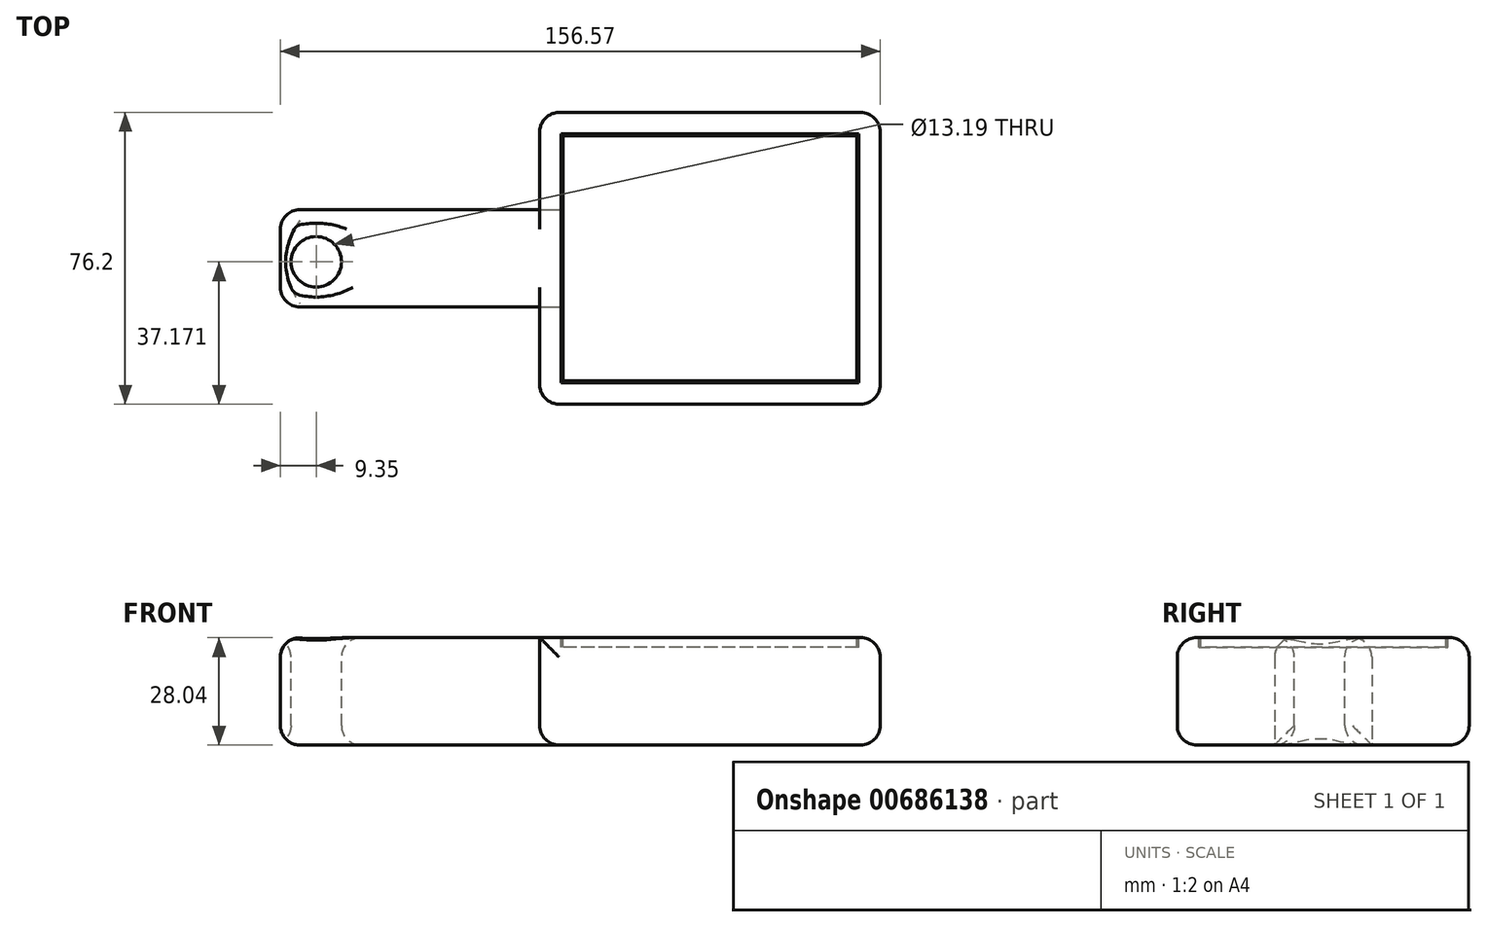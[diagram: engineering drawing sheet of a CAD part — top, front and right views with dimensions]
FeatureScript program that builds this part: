
annotation { "Feature Type Name" : "Feature", "Feature Type Description" : "" }
export const myFeature = defineFeature(function(context is Context, id is Id, definition is map)
    precondition{}
    {
        {
            var Q0;
            Q0=qCreatedBy(makeId("Front.planeOp"),FACE);
            var sketch = newSketch(context, id + "F0", { "sketchPlane" : qUnion([Q0])});
            skLineSegment(sketch, "E0.bottom", {"start": v(-47.2, 28.04) * mm, "end": v(58.57, 28.04) * mm});
            skLineSegment(sketch, "E0.top", {"start": v(-47.2, 0) * mm, "end": v(58.57, 0) * mm});
            skLineSegment(sketch, "E0.left", {"start": v(-47.2, 28.04) * mm, "end": v(-47.2, 0) * mm});
            skLineSegment(sketch, "E0.right", {"start": v(58.57, 28.04) * mm, "end": v(58.57, 0) * mm});
            skSolve(sketch);
        }
        {
            var Q0;
            Q0=makeQuery(id+"F0.imprint","IMPRINT",FACE,{"disambiguationData":[TD([[makeQuery(id+"F0.imprint","IMPRINT",EDGE,{"derivedFrom":sQuery(id+"F0.wireOp",EDGE,"E0.bottom")}),-1.0]])]});
            extrude(context, id + "F1", {"entities" : qUnion([Q0]), "depth" : 25.4 * mm, "offsetDistance" : 25.4 * mm});
        }
        {
            var Q0;
            Q0=makeQuery(id+"F1.opExtrude","CAP_FACE",FACE,{"disambiguationData":[OSD([sQuery(id+"F0.wireOp",EDGE,"E0.bottom"),sQuery(id+"F0.wireOp",EDGE,"E0.top"),sQuery(id+"F0.wireOp",EDGE,"E0.left"),sQuery(id+"F0.wireOp",EDGE,"E0.right")])],"isStart":false});
            var sketch = newSketch(context, id + "F2", { "sketchPlane" : qUnion([Q0])});
            skLineSegment(sketch, "E1", {"start": v(20.5, 28.04) * mm, "end": v(20.5, 0) * mm});
            skSolve(sketch);
        }
        {
            var Q0;
            Q0=makeQuery(id+"F1.opExtrude","SWEPT_FACE",FACE,{"disambiguationData":[OSD([sQuery(id+"F0.wireOp",EDGE,"E0.bottom")])]});
            var sketch = newSketch(context, id + "F3", { "sketchPlane" : qUnion([Q0])});
            skLineSegment(sketch, "E2", {"start": v(20.5, -25.4) * mm, "end": v(20.5, 0) * mm});
            skSolve(sketch);
        }
        {
            var Q0;
            Q0=makeQuery(id+"F1.opExtrude","CAP_FACE",FACE,{"disambiguationData":[OSD([sQuery(id+"F0.wireOp",EDGE,"E0.bottom"),sQuery(id+"F0.wireOp",EDGE,"E0.top"),sQuery(id+"F0.wireOp",EDGE,"E0.left"),sQuery(id+"F0.wireOp",EDGE,"E0.right")])],"isStart":true});
            var sketch = newSketch(context, id + "F4", { "sketchPlane" : qUnion([Q0])});
            skLineSegment(sketch, "E3", {"start": v(-20.5, 28.04) * mm, "end": v(-20.5, 0) * mm});
            skSolve(sketch);
        }
        {
            var Q0;
            {var subQ0=sQuery(id+"F2.wireOp",EDGE,"E1");Q0=makeQuery(id+"F2.imprint","IMPRINT",FACE,{"disambiguationData":[TD([[makeQuery(id+"F2.imprint","IMPRINT",EDGE,{"derivedFrom":subQ0}),1.0]])]});}
            extrude(context, id + "F5", {"entities" : qUnion([Q0]), "operationType" : NewBodyOperationType.ADD, "depth" : 25.4 * mm, "offsetDistance" : 25.4 * mm});
        }
        {
            var Q0;
            {var subQ0=sQuery(id+"F4.wireOp",EDGE,"E3");Q0=makeQuery(id+"F4.imprint","IMPRINT",FACE,{"disambiguationData":[TD([[makeQuery(id+"F4.imprint","IMPRINT",EDGE,{"derivedFrom":subQ0}),-1.0]])]});}
            extrude(context, id + "F6", {"entities" : qUnion([Q0]), "operationType" : NewBodyOperationType.ADD, "depth" : 25.4 * mm, "offsetDistance" : 25.4 * mm});
        }
        {
            var Q0;
            {var subQ0=sQuery(id+"F0.wireOp",EDGE,"E0.right");Q0=makeQuery(id+"F6.boolean.opBoolean","MERGE",FACE,{"derivedFrom":[makeQuery(id+"F5.boolean.opBoolean","MERGE",FACE,{"derivedFrom":[makeQuery(id+"F1.opExtrude","SWEPT_FACE",FACE,{"disambiguationData":[OSD([subQ0])]}),makeQuery(id+"F5.opExtrude","SWEPT_FACE",FACE,{"disambiguationData":[OSD([subQ0])]})]}),makeQuery(id+"F6.opExtrude","SWEPT_FACE",FACE,{"disambiguationData":[OSD([subQ0])]})]});}
            extrude(context, id + "F7", {"entities" : qUnion([Q0]), "operationType" : NewBodyOperationType.ADD, "depth" : 50.8 * mm, "offsetDistance" : 25.4 * mm});
        }
        {
            var Q0;
            {var subQ0=sQuery(id+"F3.wireOp",EDGE,"E2");Q0=makeQuery(id+"F3.imprint","IMPRINT",FACE,{"disambiguationData":[TD([[makeQuery(id+"F3.imprint","IMPRINT",EDGE,{"derivedFrom":subQ0}),1.0]])]});}
            var sketch = newSketch(context, id + "F8", { "sketchPlane" : qUnion([Q0])});
            skCircle(sketch, "E4", {"center": v(-37.85, -13.63) * mm, "radius": 6.6 * mm});
            skSolve(sketch);
        }
        {
            var Q0;
            Q0=makeQuery(id+"F8.imprint","IMPRINT",FACE,{"disambiguationData":[TD([[makeQuery(id+"F8.imprint","IMPRINT",EDGE,{"derivedFrom":sQuery(id+"F8.wireOp",EDGE,"E4")}),1.0]])]});
            extrude(context, id + "F9", {"entities" : qUnion([Q0]), "operationType" : NewBodyOperationType.REMOVE, "endBound" : BoundingType.THROUGH_ALL, "oppositeDirection" : true, "depth" : 25.4 * mm, "offsetDistance" : 25.4 * mm});
        }
        {
            var Q0;
            Q0=makeQuery(id+"F9.boolean.opBoolean","COPY",FACE,{"derivedFrom":makeQuery(id+"F9.opExtrude","SWEPT_FACE",FACE,{"disambiguationData":[OSD([sQuery(id+"F8.wireOp",EDGE,"E4")])]})});
            var Q1;
            Q1=makeQuery(id+"F1.opExtrude","CAP_EDGE",EDGE,{"disambiguationData":[OSD([sQuery(id+"F0.wireOp",EDGE,"E0.bottom")])],"isStart":true});
            var Q2;
            Q2=makeQuery(id+"F1.opExtrude","SWEPT_EDGE",EDGE,{"disambiguationData":[OSD([sQuery(id+"F0.wireOp",EDGE,"E0.bottom"),sQuery(id+"F0.wireOp",EDGE,"E0.left")])]});
            var Q3;
            Q3=makeQuery(id+"F1.opExtrude","CAP_EDGE",EDGE,{"disambiguationData":[OSD([sQuery(id+"F0.wireOp",EDGE,"E0.left")])],"isStart":true});
            var Q4;
            Q4=makeQuery(id+"F1.opExtrude","CAP_EDGE",EDGE,{"disambiguationData":[OSD([sQuery(id+"F0.wireOp",EDGE,"E0.left")])],"isStart":false});
            var Q5;
            Q5=makeQuery(id+"F1.opExtrude","SWEPT_EDGE",EDGE,{"disambiguationData":[OSD([sQuery(id+"F0.wireOp",EDGE,"E0.top"),sQuery(id+"F0.wireOp",EDGE,"E0.left")])]});
            var Q6;
            Q6=makeQuery(id+"F1.opExtrude","CAP_EDGE",EDGE,{"disambiguationData":[OSD([sQuery(id+"F0.wireOp",EDGE,"E0.bottom")])],"isStart":false});
            var Q7;
            Q7=makeQuery(id+"F5.opExtrude","CAP_EDGE",EDGE,{"disambiguationData":[OSD([sQuery(id+"F2.wireOp",EDGE,"E1")])],"isStart":true});
            var Q8;
            Q8=makeQuery(id+"F6.opExtrude","CAP_EDGE",EDGE,{"disambiguationData":[OSD([sQuery(id+"F4.wireOp",EDGE,"E3")])],"isStart":true});
            var Q9;
            Q9=makeQuery(id+"F6.opExtrude","CAP_EDGE",EDGE,{"disambiguationData":[OSD([sQuery(id+"F4.wireOp",EDGE,"E3")])],"isStart":false});
            var Q10;
            Q10=makeQuery(id+"F6.opExtrude","SWEPT_EDGE",EDGE,{"disambiguationData":[OSD([sQuery(id+"F0.wireOp",EDGE,"E0.top"),sQuery(id+"F4.wireOp",EDGE,"E3")])]});
            var Q11;
            Q11=makeQuery(id+"F5.opExtrude","CAP_EDGE",EDGE,{"disambiguationData":[OSD([sQuery(id+"F2.wireOp",EDGE,"E1")])],"isStart":false});
            var Q12;
            Q12=makeQuery(id+"F5.opExtrude","SWEPT_EDGE",EDGE,{"disambiguationData":[OSD([sQuery(id+"F0.wireOp",EDGE,"E0.top"),sQuery(id+"F2.wireOp",EDGE,"E1")])]});
            var Q13;
            {var subQ0=sQuery(id+"F0.wireOp",EDGE,"E0.right");var subQ1=sQuery(id+"F0.wireOp",EDGE,"E0.top");Q13=makeQuery(id+"F7.boolean.opBoolean","MERGE",EDGE,{"derivedFrom":[makeQuery(id+"F5.opExtrude","CAP_EDGE",EDGE,{"disambiguationData":[OSD([subQ1])],"isStart":false}),makeQuery(id+"F7.opExtrude","SWEPT_EDGE",EDGE,{"disambiguationData":[OSD([subQ1,subQ0]),TDD([makeQuery(id+"F5.opExtrude","CAP_VERTEX",VERTEX,{"disambiguationData":[OSD([subQ1,subQ0])],"isStart":false})])]})]});}
            var Q14;
            {var subQ0=sQuery(id+"F0.wireOp",EDGE,"E0.right");var subQ1=sQuery(id+"F0.wireOp",EDGE,"E0.bottom");Q14=makeQuery(id+"F7.boolean.opBoolean","MERGE",EDGE,{"derivedFrom":[makeQuery(id+"F5.opExtrude","CAP_EDGE",EDGE,{"disambiguationData":[OSD([subQ1])],"isStart":false}),makeQuery(id+"F7.opExtrude","SWEPT_EDGE",EDGE,{"disambiguationData":[OSD([subQ1,subQ0]),TDD([makeQuery(id+"F5.opExtrude","CAP_VERTEX",VERTEX,{"disambiguationData":[OSD([subQ1,subQ0])],"isStart":false})])]})]});}
            var Q15;
            {var subQ0=sQuery(id+"F0.wireOp",EDGE,"E0.right");Q15=makeQuery(id+"F7.opExtrude","CAP_EDGE",EDGE,{"disambiguationData":[OSD([subQ0]),TDD([makeQuery(id+"F5.opExtrude","CAP_EDGE",EDGE,{"disambiguationData":[OSD([subQ0])],"isStart":false})])],"isStart":false});}
            var Q16;
            Q16=makeQuery(id+"F7.opExtrude","CAP_EDGE",EDGE,{"disambiguationData":[OSD([sQuery(id+"F0.wireOp",EDGE,"E0.top"),sQuery(id+"F0.wireOp",EDGE,"E0.right")])],"isStart":false});
            var Q17;
            Q17=makeQuery(id+"F7.opExtrude","CAP_EDGE",EDGE,{"disambiguationData":[OSD([sQuery(id+"F0.wireOp",EDGE,"E0.bottom"),sQuery(id+"F0.wireOp",EDGE,"E0.right")])],"isStart":false});
            var Q18;
            {var subQ0=sQuery(id+"F0.wireOp",EDGE,"E0.right");Q18=makeQuery(id+"F7.opExtrude","CAP_EDGE",EDGE,{"disambiguationData":[OSD([subQ0]),TDD([makeQuery(id+"F6.opExtrude","CAP_EDGE",EDGE,{"disambiguationData":[OSD([subQ0])],"isStart":false})])],"isStart":false});}
            var Q19;
            {var subQ0=sQuery(id+"F0.wireOp",EDGE,"E0.right");var subQ1=sQuery(id+"F0.wireOp",EDGE,"E0.top");Q19=makeQuery(id+"F7.boolean.opBoolean","MERGE",EDGE,{"derivedFrom":[makeQuery(id+"F6.opExtrude","CAP_EDGE",EDGE,{"disambiguationData":[OSD([subQ1])],"isStart":false}),makeQuery(id+"F7.opExtrude","SWEPT_EDGE",EDGE,{"disambiguationData":[OSD([subQ1,subQ0]),TDD([makeQuery(id+"F6.opExtrude","CAP_VERTEX",VERTEX,{"disambiguationData":[OSD([subQ1,subQ0])],"isStart":false})])]})]});}
            var Q20;
            {var subQ0=sQuery(id+"F0.wireOp",EDGE,"E0.right");var subQ1=sQuery(id+"F0.wireOp",EDGE,"E0.bottom");Q20=makeQuery(id+"F7.boolean.opBoolean","MERGE",EDGE,{"derivedFrom":[makeQuery(id+"F6.opExtrude","CAP_EDGE",EDGE,{"disambiguationData":[OSD([subQ1])],"isStart":false}),makeQuery(id+"F7.opExtrude","SWEPT_EDGE",EDGE,{"disambiguationData":[OSD([subQ1,subQ0]),TDD([makeQuery(id+"F6.opExtrude","CAP_VERTEX",VERTEX,{"disambiguationData":[OSD([subQ1,subQ0])],"isStart":false})])]})]});}
            fillet(context, id + "F10", {"entities" : qUnion([Q0, Q1, Q2, Q3, Q4, Q5, Q6, Q7, Q8, Q9, Q10, Q11, Q12, Q13, Q14, Q15, Q16, Q17, Q18, Q19, Q20]), "radius" : 5.08 * mm, "tangentPropagation" : true, "allowEdgeOverflow" : false});
        }
        {
            var Q0;
            {var subQ0=sQuery(id+"F0.wireOp",EDGE,"E0.bottom");Q0=makeQuery(id+"F7.boolean.opBoolean","MERGE",FACE,{"derivedFrom":[makeQuery(id+"F6.boolean.opBoolean","MERGE",FACE,{"derivedFrom":[makeQuery(id+"F5.boolean.opBoolean","MERGE",FACE,{"derivedFrom":[makeQuery(id+"F1.opExtrude","SWEPT_FACE",FACE,{"disambiguationData":[OSD([subQ0])]}),makeQuery(id+"F5.opExtrude","SWEPT_FACE",FACE,{"disambiguationData":[OSD([subQ0])]})]}),makeQuery(id+"F6.opExtrude","SWEPT_FACE",FACE,{"disambiguationData":[OSD([subQ0])]})]}),makeQuery(id+"F7.opExtrude","SWEPT_FACE",FACE,{"disambiguationData":[OSD([subQ0,sQuery(id+"F0.wireOp",EDGE,"E0.right")])]})]});}
            var sketch = newSketch(context, id + "F11", { "sketchPlane" : qUnion([Q0])});
            skLineSegment(sketch, "E5.0", {"start": v(103.78, 19.81) * mm, "end": v(26.08, 19.81) * mm});
            skLineSegment(sketch, "E6.0", {"start": v(103.78, -45.21) * mm, "end": v(103.78, 19.81) * mm});
            skLineSegment(sketch, "E6.1", {"start": v(26.08, -45.21) * mm, "end": v(103.78, -45.21) * mm});
            skLineSegment(sketch, "E6.2", {"start": v(26.08, -30.48) * mm, "end": v(26.08, -45.21) * mm});
            skLineSegment(sketch, "E7", {"start": v(26.08, -30.48) * mm, "end": v(26.08, 19.81) * mm});
            skLineSegment(sketch, "E8.0", {"start": v(26.59, -30.48) * mm, "end": v(26.59, 19.3) * mm});
            skLineSegment(sketch, "E8.1", {"start": v(103.27, 19.3) * mm, "end": v(26.59, 19.3) * mm});
            skLineSegment(sketch, "E8.2", {"start": v(26.59, -30.48) * mm, "end": v(26.59, -44.7) * mm});
            skLineSegment(sketch, "E8.3", {"start": v(26.59, -44.7) * mm, "end": v(103.27, -44.7) * mm});
            skLineSegment(sketch, "E8.4", {"start": v(103.27, -44.7) * mm, "end": v(103.27, 19.3) * mm});
            skSolve(sketch);
        }
        {
            var Q0;
            Q0=makeQuery(id+"F11.imprint","IMPRINT",FACE,{"disambiguationData":[TD([[makeQuery(id+"F11.imprint","IMPRINT",EDGE,{"derivedFrom":sQuery(id+"F11.wireOp",EDGE,"E5.0")}),1.0]])]});
            extrude(context, id + "F12", {"entities" : qUnion([Q0]), "operationType" : NewBodyOperationType.REMOVE, "oppositeDirection" : true, "depth" : 2.54 * mm, "offsetDistance" : 25.4 * mm});
        }
    });
